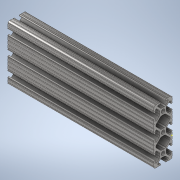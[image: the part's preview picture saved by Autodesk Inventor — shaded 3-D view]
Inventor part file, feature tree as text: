
AUTODESK INVENTOR PART (.ipt)
format: ipt  version: 2020 (Build 240168000, 168)  size: 377,344 bytes
history: native  units: in
note: dims shown in document units (in); Inventor stores cm internally (conversion verified against a paired STEP export)
features: sketch x2, extrude x1
ambient origin geometry x8: Origin, YZ Plane, XZ Plane, XY Plane, X Axis, Y Axis, Z Axis, Center Point
bodies: Solid1 (feature_tree)
feature tree (3):
  extrude  "Extrusion1"  [1 undecoded]
  sketch  "Sketch2"
  sketch  "Sketch1"  dims[d0=8.0in d1=0.0in]
note: 1 required parameter value undecoded (feature->parameter linkage not recoverable at this tier; creation-order binding heuristic only, values carry confidence <= 0.55)
